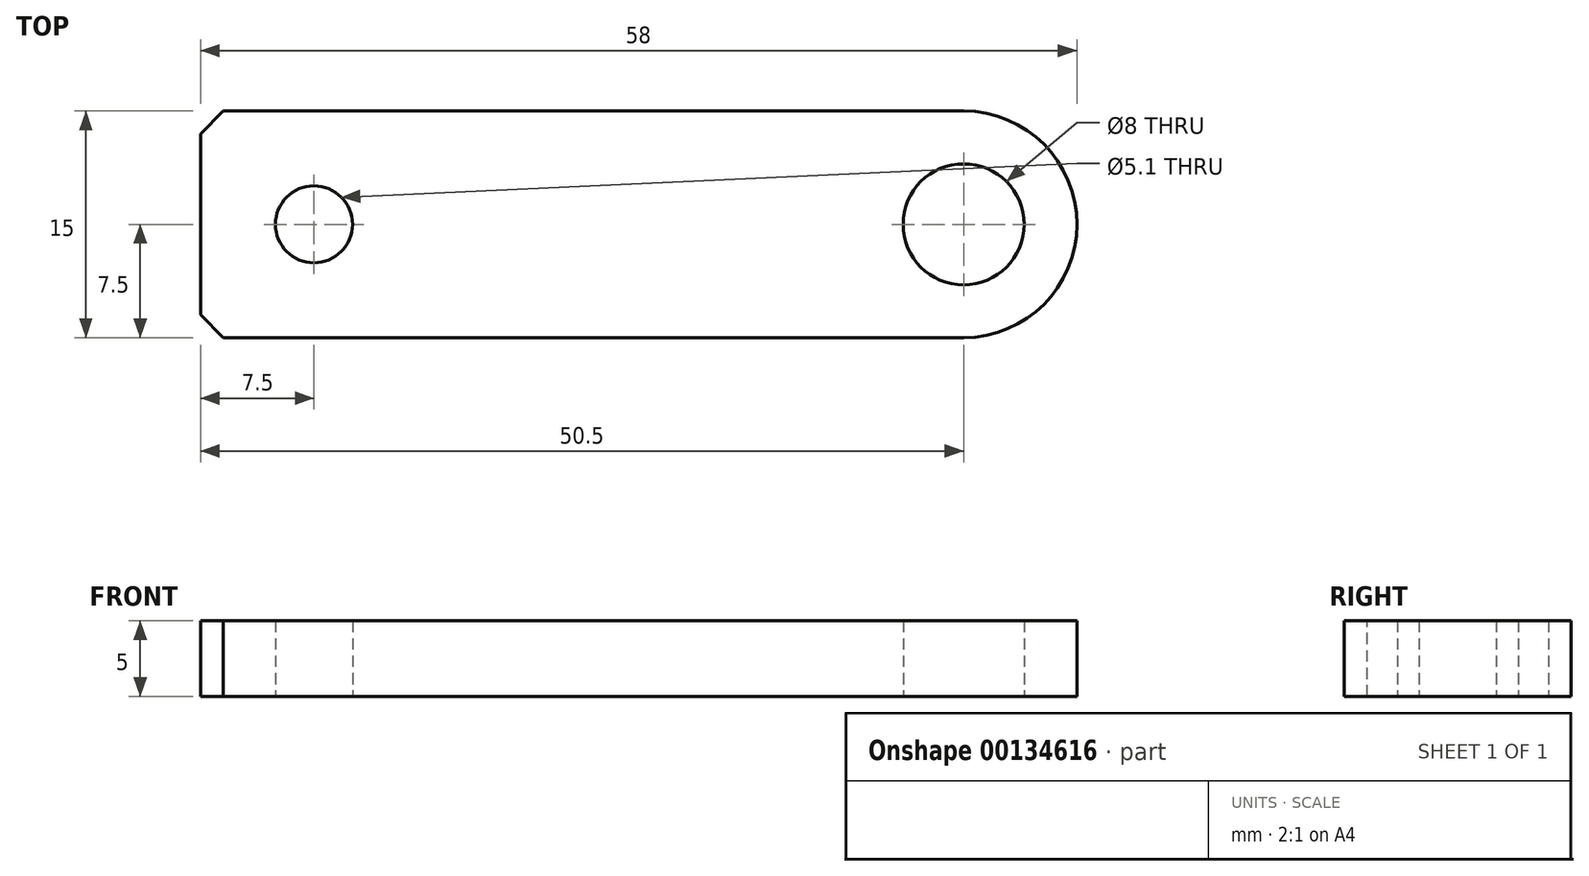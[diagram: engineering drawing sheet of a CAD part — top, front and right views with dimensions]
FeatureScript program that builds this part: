
annotation { "Feature Type Name" : "Feature", "Feature Type Description" : "" }
export const myFeature = defineFeature(function(context is Context, id is Id, definition is map)
    precondition{}
    {
        {
            var Q0;
            Q0=qCreatedBy(makeId("Top.planeOp"),FACE);
            var sketch = newSketch(context, id + "F0", { "sketchPlane" : qUnion([Q0])});
            skLineSegment(sketch, "E0.bottom", {"start": v(21.5, -7.5) * mm, "end": v(-29, -7.5) * mm});
            skLineSegment(sketch, "E0.top", {"start": v(21.5, 7.5) * mm, "end": v(-29, 7.5) * mm});
            skLineSegment(sketch, "E0.left", {"start": v(29, 0) * mm, "end": v(29, 0) * mm});
            skLineSegment(sketch, "E0.right", {"start": v(-29, -7.5) * mm, "end": v(-29, 7.5) * mm});
            skPoint(sketch, "E0.middle", {"position": v(0, 0) * mm});
            skPoint(sketch, "E1.visualSharp", {"position": v(29, 7.5) * mm});
            skArc(sketch, "E1.filletArc", {"start": v(29, 0) * mm, "mid": v(26.8, 5.3) * mm, "end": v(21.5, 7.5) * mm});
            skPoint(sketch, "E2.visualSharp", {"position": v(29, -7.5) * mm});
            skArc(sketch, "E2.filletArc", {"start": v(21.5, -7.5) * mm, "mid": v(26.8, -5.3) * mm, "end": v(29, 0) * mm});
            skCircle(sketch, "E3", {"center": v(21.5, 0) * mm, "radius": 4 * mm});
            skCircle(sketch, "E4", {"center": v(-21.5, 0) * mm, "radius": 2.55 * mm});
            skPoint(sketch, "E4.centerSnap0", {"position": v(-29, 0) * mm});
            skSolve(sketch);
        }
        {
            var Q0;
            Q0=makeQuery(id+"F0.imprint","IMPRINT",FACE,{"disambiguationData":[TD([[makeQuery(id+"F0.imprint","IMPRINT",EDGE,{"derivedFrom":sQuery(id+"F0.wireOp",EDGE,"E0.bottom")}),-1.0]])]});
            extrude(context, id + "F1", {"entities" : qUnion([Q0]), "depth" : 5 * mm});
        }
        {
            var Q0;
            Q0=makeQuery(id+"F1.opExtrude","SWEPT_EDGE",EDGE,{"disambiguationData":[OSD([sQuery(id+"F0.wireOp",EDGE,"E0.top"),sQuery(id+"F0.wireOp",EDGE,"E0.right")])]});
            var Q1;
            Q1=makeQuery(id+"F1.opExtrude","SWEPT_EDGE",EDGE,{"disambiguationData":[OSD([sQuery(id+"F0.wireOp",EDGE,"E0.bottom"),sQuery(id+"F0.wireOp",EDGE,"E0.right")])]});
            chamfer(context, id + "F2", {"entities" : qUnion([Q0, Q1]), "width" : 1.5 * mm, "tangentPropagation" : true});
        }
    });
